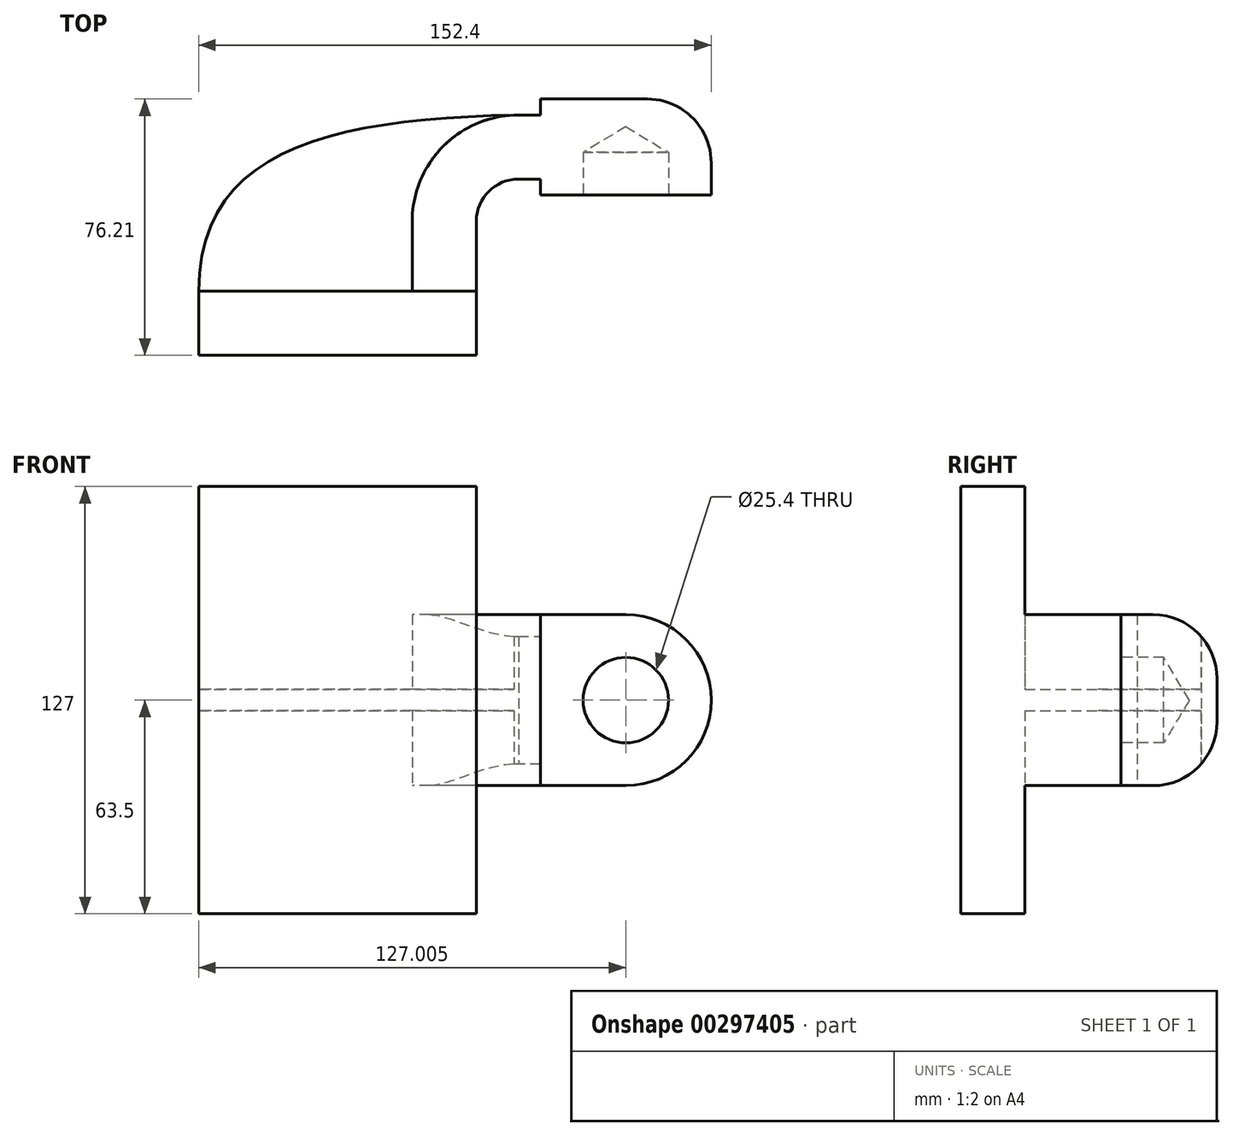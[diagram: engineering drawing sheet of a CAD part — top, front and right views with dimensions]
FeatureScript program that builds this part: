
annotation { "Feature Type Name" : "Feature", "Feature Type Description" : "" }
export const myFeature = defineFeature(function(context is Context, id is Id, definition is map)
    precondition{}
    {
        {
            var Q0;
            Q0=qCreatedBy(makeId("Top.planeOp"),FACE);
            var sketch = newSketch(context, id + "F0", { "sketchPlane" : qUnion([Q0])});
            skLineSegment(sketch, "E0.bottom", {"start": v(41.28, 9.52) * mm, "end": v(-41.28, 9.52) * mm});
            skLineSegment(sketch, "E0.top", {"start": v(41.28, -9.53) * mm, "end": v(-41.28, -9.53) * mm});
            skLineSegment(sketch, "E0.left", {"start": v(41.28, 9.52) * mm, "end": v(41.28, -9.53) * mm});
            skLineSegment(sketch, "E0.right", {"start": v(-41.28, 9.52) * mm, "end": v(-41.28, -9.53) * mm});
            skPoint(sketch, "E0.middle", {"position": v(0, 0) * mm});
            skLineSegment(sketch, "E1.bottom", {"start": v(111.13, 38.1) * mm, "end": v(60.33, 38.1) * mm});
            skLineSegment(sketch, "E1.top", {"start": v(111.13, 66.67) * mm, "end": v(60.33, 66.67) * mm});
            skLineSegment(sketch, "E1.left", {"start": v(111.13, 38.1) * mm, "end": v(111.13, 66.68) * mm});
            skLineSegment(sketch, "E1.right", {"start": v(60.33, 38.1) * mm, "end": v(60.33, 66.68) * mm});
            skPoint(sketch, "E1.middle", {"position": v(85.73, 52.39) * mm});
            skLineSegment(sketch, "E2", {"start": v(41.28, 9.52) * mm, "end": v(41.28, 30.32) * mm});
            skArc(sketch, "E3", {"start": v(41.28, 30.32) * mm, "mid": v(44.95, 39.2) * mm, "end": v(53.83, 42.88) * mm});
            skLineSegment(sketch, "E4", {"start": v(53.83, 42.88) * mm, "end": v(85.73, 42.88) * mm});
            skLineSegment(sketch, "E5.0", {"start": v(53.83, 61.93) * mm, "end": v(85.73, 61.93) * mm});
            skArc(sketch, "E5.1", {"start": v(22.23, 30.32) * mm, "mid": v(31.48, 52.67) * mm, "end": v(53.83, 61.93) * mm});
            skLineSegment(sketch, "E5.2", {"start": v(22.23, 9.52) * mm, "end": v(22.23, 30.32) * mm});
            skLineSegment(sketch, "E6", {"start": v(85.73, 38.1) * mm, "end": v(85.73, 66.67) * mm});
            skFitSpline(sketch, "E7", {"points": [v(-41.28, 9.52) * mm, v(53.83, 61.93) * mm], "startDerivative": vector(-0.1, 129.4) * mm, "endDerivative": vector(161.5, 3.35) * mm});
            skSolve(sketch);
        }
        {
            var Q0;
            Q0=makeQuery(id+"F0.imprint","IMPRINT",FACE,{"disambiguationData":[TD([[makeQuery(id+"F0.imprint","IMPRINT",EDGE,{"derivedFrom":sQuery(id+"F0.wireOp",EDGE,"E0.top")}),-1.0]])]});
            extrude(context, id + "F1", {"entities" : qUnion([Q0]), "endBound" : BoundingType.SYMMETRIC, "depth" : 127 * mm});
        }
        {
            var Q0;
            {var subQ1=sQuery(id+"F0.wireOp",EDGE,"E2");Q0=makeQuery(id+"F0.imprint","IMPRINT",FACE,{"disambiguationData":[TD([[makeQuery(id+"F0.imprint","IMPRINT",EDGE,{"derivedFrom":subQ1}),1.0]])]});}
            var Q1;
            {var subQ0=sQuery(id+"F0.wireOp",EDGE,"E4");var subQ1=sQuery(id+"F0.wireOp",EDGE,"E1.right");var subQ2=makeQuery(id+"F0.imprint","INTERSECT",VERTEX,{"derivedFrom":[subQ1,subQ0]});Q1=makeQuery(id+"F0.imprint","IMPRINT",FACE,{"disambiguationData":[TD([[makeQuery(id+"F0.imprint","IMPRINT",EDGE,{"disambiguationData":[TD([[subQ2,-1.0]])],"derivedFrom":subQ1}),-1.0]])]});}
            var Q2;
            {var subQ0=sQuery(id+"F0.wireOp",EDGE,"E1.right");var subQ1=sQuery(id+"F0.wireOp",EDGE,"E1.top");var subQ2=makeQuery(id+"F0.imprint","INTERSECT",VERTEX,{"derivedFrom":[subQ1,subQ0]});Q2=makeQuery(id+"F0.imprint","IMPRINT",FACE,{"disambiguationData":[TD([[makeQuery(id+"F0.imprint","IMPRINT",EDGE,{"disambiguationData":[TD([[subQ2,1.0]])],"derivedFrom":subQ1}),1.0]])]});}
            var Q3;
            {var subQ0=sQuery(id+"F0.wireOp",EDGE,"E1.right");var subQ1=sQuery(id+"F0.wireOp",EDGE,"E1.bottom");var subQ2=makeQuery(id+"F0.imprint","INTERSECT",VERTEX,{"derivedFrom":[subQ1,subQ0]});Q3=makeQuery(id+"F0.imprint","IMPRINT",FACE,{"disambiguationData":[TD([[makeQuery(id+"F0.imprint","IMPRINT",EDGE,{"disambiguationData":[TD([[subQ2,1.0]])],"derivedFrom":subQ1}),-1.0]])]});}
            extrude(context, id + "F2", {"entities" : qUnion([Q0, Q1, Q2, Q3]), "operationType" : NewBodyOperationType.ADD, "endBound" : BoundingType.SYMMETRIC, "depth" : 50.8 * mm});
        }
        {
            var Q0;
            {var subQ3=sQuery(id+"F0.wireOp",EDGE,"E5.2");Q0=makeQuery(id+"F0.imprint","IMPRINT",FACE,{"disambiguationData":[TD([[makeQuery(id+"F0.imprint","IMPRINT",EDGE,{"derivedFrom":subQ3}),1.0]])]});}
            extrude(context, id + "F3", {"entities" : qUnion([Q0]), "operationType" : NewBodyOperationType.ADD, "endBound" : BoundingType.SYMMETRIC, "depth" : 6.35 * mm});
        }
        {
            var Q0;
            {var subQ0=sQuery(id+"F0.wireOp",EDGE,"E1.left");Q0=makeQuery(id+"F0.imprint","IMPRINT",FACE,{"disambiguationData":[TD([[makeQuery(id+"F0.imprint","IMPRINT",EDGE,{"derivedFrom":subQ0}),1.0]])]});}
            var Q1;
            Q1=sQuery(id+"F0.wireOp",EDGE,"E6");
            revolve(context, id + "F4", {"operationType" : NewBodyOperationType.ADD, "entities" : qUnion([Q0]), "axis" : qUnion([Q1]), "revolveType" : RevolveType.FULL});
        }
        {
            var Q0;
            Q0=makeQuery(id+"F4.opRevolve","SWEPT_EDGE",EDGE,{"disambiguationData":[OSD([sQuery(id+"F0.wireOp",EDGE,"E1.top"),sQuery(id+"F0.wireOp",EDGE,"E1.left")])]});
            fillet(context, id + "F5", {"entities" : qUnion([Q0]), "radius" : 19 * mm, "tangentPropagation" : true, "allowEdgeOverflow" : false});
        }
        {
            var Q0;
            {var subQ0=sQuery(id+"F0.wireOp",EDGE,"E1.bottom");Q0=makeQuery(id+"F4.boolean.opBoolean","MERGE",FACE,{"derivedFrom":[makeQuery(id+"F2.opExtrude","SWEPT_FACE",FACE,{"disambiguationData":[OSD([subQ0])]}),makeQuery(id+"F4.opRevolve","SWEPT_FACE",FACE,{"disambiguationData":[OSD([subQ0])]})]});}
            var sketch = newSketch(context, id + "F6", { "sketchPlane" : qUnion([Q0])});
            skPoint(sketch, "E8", {"position": v(85.73, 0) * mm});
            skSolve(sketch);
        }
        {
            var Q0;
            Q0=sQuery(id+"F6.wireOp",VERTEX,"E8");
            var Q1;
            Q1=makeQuery(id+"F1.opExtrude","SWEPT_BODY",BODY,{"disambiguationData":[OSD([sQuery(id+"F0.wireOp",EDGE,"E0.bottom"),sQuery(id+"F0.wireOp",EDGE,"E0.top"),sQuery(id+"F0.wireOp",EDGE,"E0.left"),sQuery(id+"F0.wireOp",EDGE,"E0.right")])]});
            hole(context, id + "F7", {"style" : HoleStyle.SIMPLE, "endStyle" : HoleEndStyle.BLIND, "holeDiameter" : 25.4 * mm, "holeDepth" : 12.7 * mm, "tappedDepth" : 12.7 * mm, "tapClearance" : 3, "locations" : qUnion([Q0]), "scope" : qUnion([Q1])});
        }
    });
